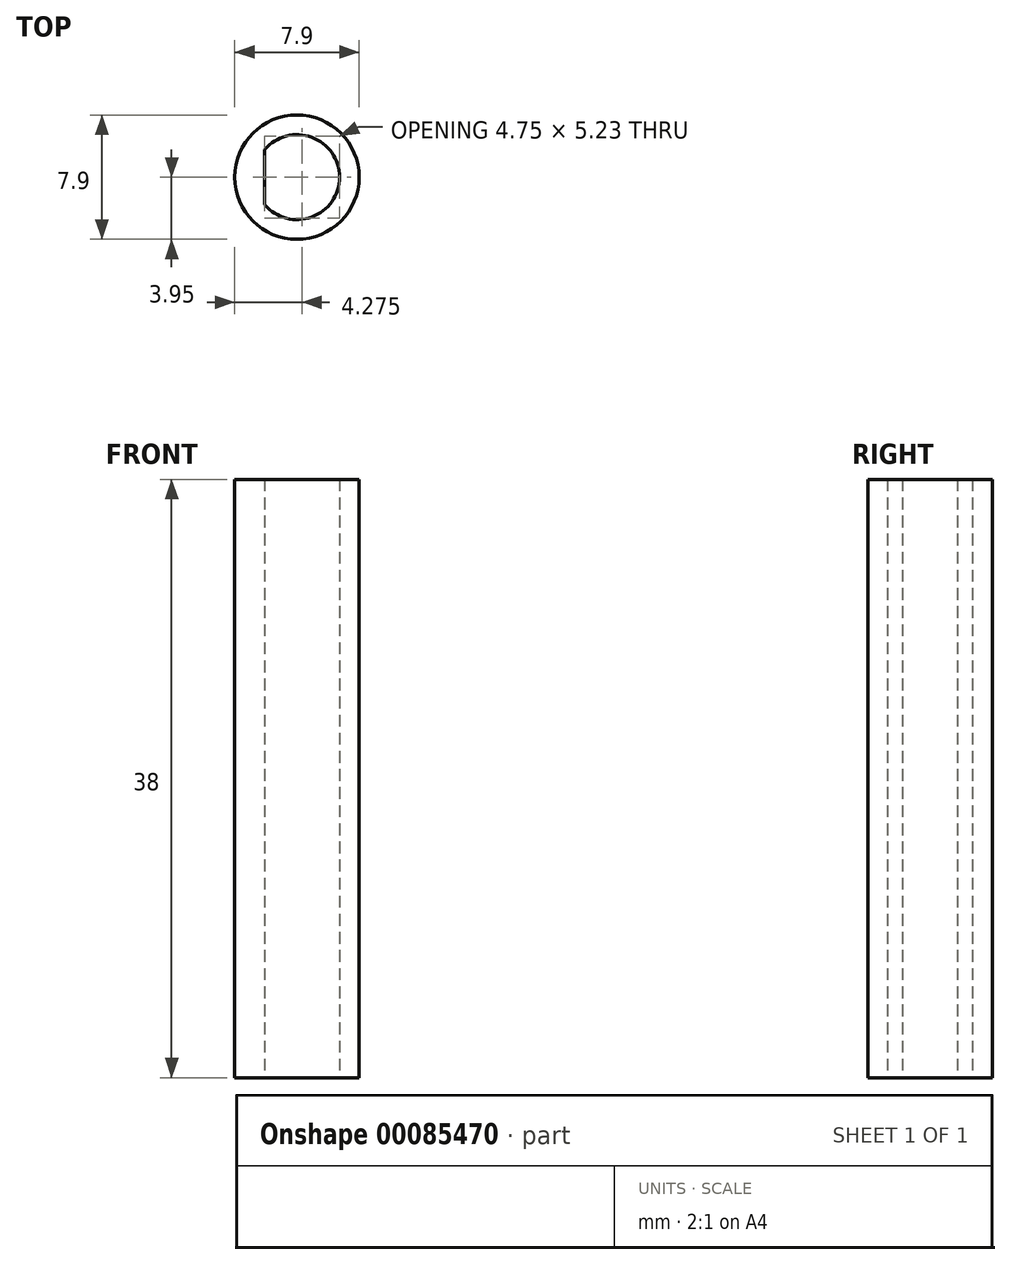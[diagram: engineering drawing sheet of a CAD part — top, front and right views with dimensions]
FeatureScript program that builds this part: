
annotation { "Feature Type Name" : "Feature", "Feature Type Description" : "" }
export const myFeature = defineFeature(function(context is Context, id is Id, definition is map)
    precondition{}
    {
        {
            var Q0;
            Q0=qCreatedBy(makeId("Top.planeOp"),FACE);
            var sketch = newSketch(context, id + "F0", { "sketchPlane" : qUnion([Q0])});
            skCircle(sketch, "E0", {"center": v(0, 0) * mm, "radius": 2.7 * mm});
            skCircle(sketch, "E1", {"center": v(0, 0) * mm, "radius": 3.95 * mm});
            skLineSegment(sketch, "E2", {"start": v(-2.05, 1.76) * mm, "end": v(-2.05, -1.76) * mm});
            skLineSegment(sketch, "E3", {"start": v(-2.05, 0) * mm, "end": v(2.7, 0) * mm, "construction": true});
            skSolve(sketch);
        }
        {
            var Q0;
            Q0=makeQuery(id+"F0.imprint","IMPRINT",FACE,{"disambiguationData":[TD([[makeQuery(id+"F0.imprint","IMPRINT",EDGE,{"derivedFrom":sQuery(id+"F0.wireOp",EDGE,"E0")}),-1.0]])]});
            var Q1;
            {var subQ0=sQuery(id+"F0.wireOp",EDGE,"E2");Q1=makeQuery(id+"F0.imprint","IMPRINT",FACE,{"disambiguationData":[TD([[makeQuery(id+"F0.imprint","IMPRINT",EDGE,{"derivedFrom":subQ0}),-1.0]])]});}
            extrude(context, id + "F1", {"entities" : qUnion([Q0, Q1]), "depth" : 38 * mm});
        }
    });
